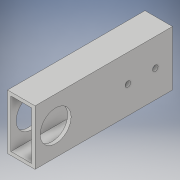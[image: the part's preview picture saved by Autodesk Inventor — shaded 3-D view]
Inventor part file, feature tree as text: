
AUTODESK INVENTOR PART (.ipt)
format: ipt  version: 2018 (Build 220112000, 112)  size: 122,880 bytes
history: native  units: in
note: dims shown in document units (in); Inventor stores cm internally (conversion verified against a paired STEP export)
features: extrude x3, sketch x3
ambient origin geometry x8: Origin, YZ Plane, XZ Plane, XY Plane, X Axis, Y Axis, Z Axis, Center Point
bodies: Solid1 (feature_tree)
feature tree (6):
  extrude  "Extrusion1"  Depth=2.0in
  extrude  "Extrusion2"  Depth=5.0in TaperAngle=0.0deg
  extrude  "Extrusion3"  Depth=1.0in
  sketch  "Sketch1"  dims[d0=1.0in d1=2.0in]
  sketch  "Sketch2"  dims[d2=0.125in d3=5.0in d4=0.0in]
  sketch  "Sketch3"  dims[d5=4.25in d6=1.125in d7=4.0in d8=0.0in d9=0.625in d10=1.0in d11=0.2031in d12=0.2031in d13=4.0in d14=0.0in]
